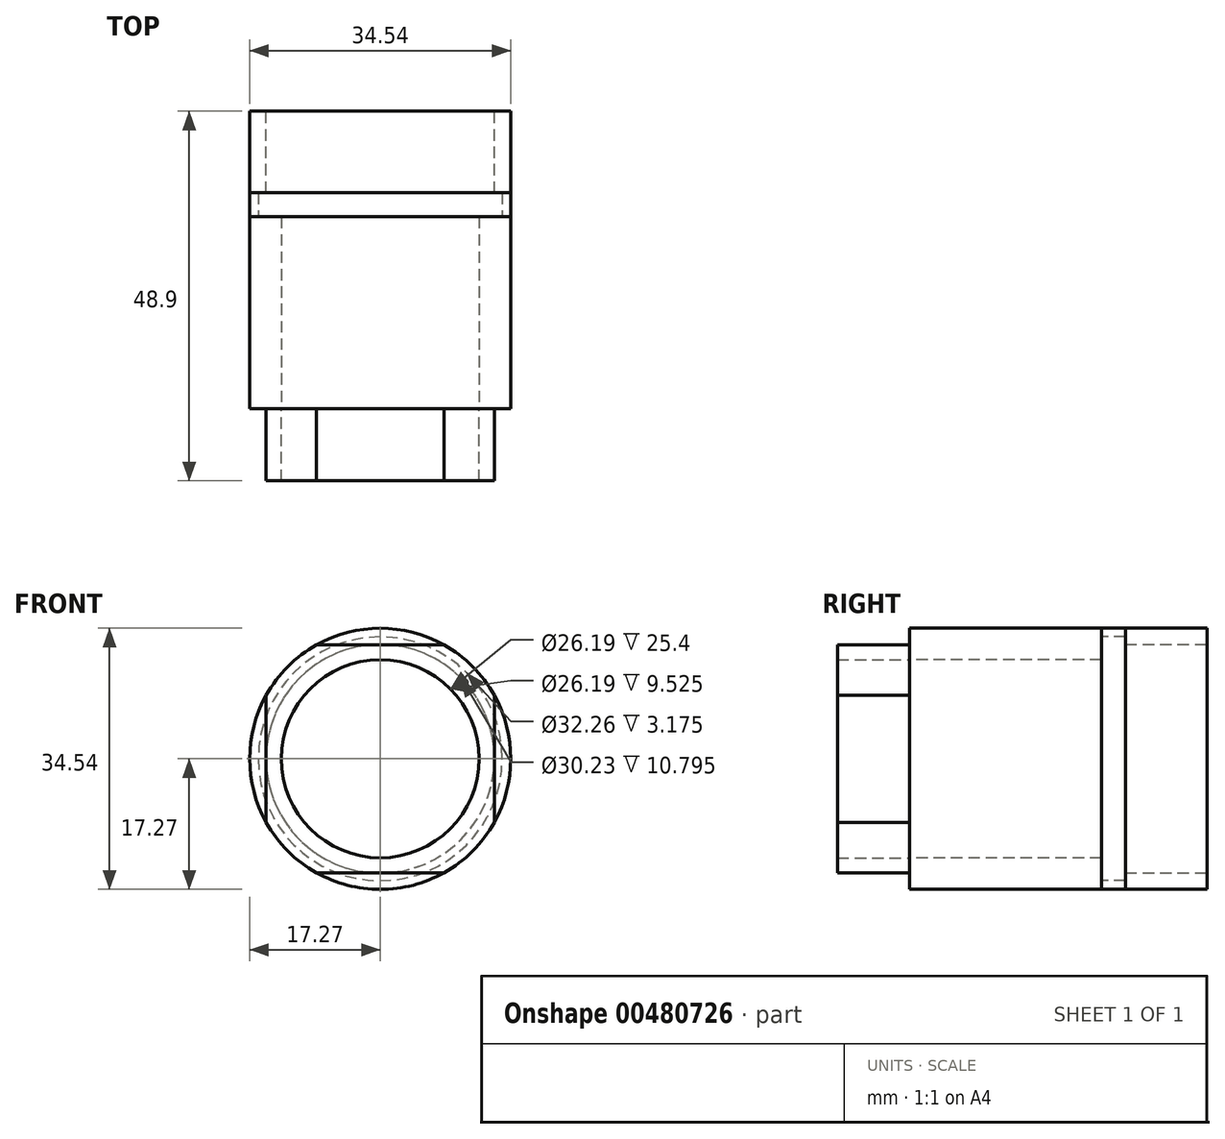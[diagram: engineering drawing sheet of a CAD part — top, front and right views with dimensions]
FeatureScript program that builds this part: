
annotation { "Feature Type Name" : "Feature", "Feature Type Description" : "" }
export const myFeature = defineFeature(function(context is Context, id is Id, definition is map)
    precondition{}
    {
        {
            var Q0;
            Q0=qCreatedBy(makeId("Front.planeOp"),FACE);
            var sketch = newSketch(context, id + "F0", { "sketchPlane" : qUnion([Q0])});
            skCircle(sketch, "E0", {"center": v(0, 0) * mm, "radius": 17.27 * mm});
            skSolve(sketch);
        }
        {
            var Q0;
            Q0 = qSketchRegion(id + "F0", true);
            extrude(context, id + "F1", {"entities" : qUnion([Q0]), "depth" : 10.8 * mm, "offsetDistance" : 25.4 * mm});
        }
        {
            var Q0;
            Q0=makeQuery(id+"F1.opExtrude","CAP_FACE",FACE,{"disambiguationData":[OSD([sQuery(id+"F0.wireOp",EDGE,"E0")])],"isStart":true});
            var sketch = newSketch(context, id + "F2", { "sketchPlane" : qUnion([Q0])});
            skCircle(sketch, "E1", {"center": v(0, 0) * mm, "radius": 15.11 * mm});
            skSolve(sketch);
        }
        {
            var Q0;
            Q0 = qSketchRegion(id + "F2", true);
            extrude(context, id + "F3", {"entities" : qUnion([Q0]), "operationType" : NewBodyOperationType.REMOVE, "endBound" : BoundingType.UP_TO_NEXT, "oppositeDirection" : true, "depth" : 25.4 * mm, "offsetDistance" : 25.4 * mm});
        }
        {
            var Q0;
            Q0=makeQuery(id+"F1.opExtrude","CAP_FACE",FACE,{"disambiguationData":[OSD([sQuery(id+"F0.wireOp",EDGE,"E0")])],"isStart":false});
            var sketch = newSketch(context, id + "F4", { "sketchPlane" : qUnion([Q0])});
            skCircle(sketch, "E2", {"center": v(0, 0) * mm, "radius": 17.27 * mm});
            skSolve(sketch);
        }
        {
            var Q0;
            Q0 = qSketchRegion(id + "F4", true);
            extrude(context, id + "F5", {"entities" : qUnion([Q0]), "depth" : 3.17 * mm, "offsetDistance" : 25.4 * mm});
        }
        {
            var Q0;
            Q0=makeQuery(id+"F5.opExtrude","CAP_FACE",FACE,{"disambiguationData":[OSD([sQuery(id+"F4.wireOp",EDGE,"E2")])],"isStart":false});
            var sketch = newSketch(context, id + "F6", { "sketchPlane" : qUnion([Q0])});
            skCircle(sketch, "E3", {"center": v(0, 0) * mm, "radius": 16.13 * mm});
            skSolve(sketch);
        }
        {
            var Q0;
            Q0 = qSketchRegion(id + "F6", true);
            extrude(context, id + "F7", {"entities" : qUnion([Q0]), "operationType" : NewBodyOperationType.REMOVE, "endBound" : BoundingType.UP_TO_NEXT, "oppositeDirection" : true, "depth" : 25.4 * mm, "offsetDistance" : 25.4 * mm});
        }
        {
            var Q0;
            Q0=makeQuery(id+"F5.opExtrude","CAP_FACE",FACE,{"disambiguationData":[OSD([sQuery(id+"F4.wireOp",EDGE,"E2")])],"isStart":false});
            var sketch = newSketch(context, id + "F8", { "sketchPlane" : qUnion([Q0])});
            skCircle(sketch, "E4", {"center": v(0, 0) * mm, "radius": 17.27 * mm});
            skSolve(sketch);
        }
        {
            var Q0;
            Q0 = qSketchRegion(id + "F8", true);
            extrude(context, id + "F9", {"entities" : qUnion([Q0]), "depth" : 25.4 * mm, "offsetDistance" : 25.4 * mm});
        }
        {
            var Q0;
            Q0=makeQuery(id+"F9.opExtrude","CAP_FACE",FACE,{"disambiguationData":[OSD([sQuery(id+"F8.wireOp",EDGE,"E4")])],"isStart":false});
            var sketch = newSketch(context, id + "F10", { "sketchPlane" : qUnion([Q0])});
            skCircle(sketch, "E5", {"center": v(0, 0) * mm, "radius": 13.1 * mm});
            skSolve(sketch);
        }
        {
            var Q0;
            Q0 = qSketchRegion(id + "F10", true);
            extrude(context, id + "F11", {"entities" : qUnion([Q0]), "operationType" : NewBodyOperationType.REMOVE, "endBound" : BoundingType.UP_TO_NEXT, "oppositeDirection" : true, "depth" : 25.4 * mm, "offsetDistance" : 25.4 * mm});
        }
        {
            var Q0;
            Q0=makeQuery(id+"F9.opExtrude","CAP_FACE",FACE,{"disambiguationData":[OSD([sQuery(id+"F8.wireOp",EDGE,"E4")])],"isStart":false});
            var sketch = newSketch(context, id + "F12", { "sketchPlane" : qUnion([Q0])});
            skCircle(sketch, "E6.cCircle", {"center": v(0, 0) * mm, "radius": 15.08 * mm, "construction": true});
            skLineSegment(sketch, "E6.0", {"start": v(15.08, 8.42) * mm, "end": v(15.08, -8.42) * mm});
            skLineSegment(sketch, "E6.1", {"start": v(8.42, -15.08) * mm, "end": v(-8.42, -15.08) * mm});
            skLineSegment(sketch, "E6.2", {"start": v(-15.08, -8.42) * mm, "end": v(-15.08, 8.42) * mm});
            skLineSegment(sketch, "E6.3", {"start": v(-8.42, 15.08) * mm, "end": v(8.42, 15.08) * mm});
            skPoint(sketch, "E6.0.midPoint", {"position": v(15.08, 0) * mm});
            skPoint(sketch, "E7", {"position": v(15.08, 8.42) * mm});
            skPoint(sketch, "E8", {"position": v(8.42, 15.08) * mm});
            skPoint(sketch, "E9", {"position": v(-8.42, 15.08) * mm});
            skPoint(sketch, "E10", {"position": v(-15.08, 8.42) * mm});
            skPoint(sketch, "E11", {"position": v(-15.08, -8.42) * mm});
            skPoint(sketch, "E12", {"position": v(-8.42, -15.08) * mm});
            skPoint(sketch, "E13", {"position": v(8.42, -15.08) * mm});
            skPoint(sketch, "E14", {"position": v(15.08, -8.42) * mm});
            skPoint(sketch, "E15.orphan", {"position": v(-15.08, 15.08) * mm});
            skPoint(sketch, "E16.orphan", {"position": v(15.08, 15.08) * mm});
            skPoint(sketch, "E17.orphan", {"position": v(15.08, -15.08) * mm});
            skPoint(sketch, "E18.orphan", {"position": v(-15.08, -15.08) * mm});
            skSolve(sketch);
        }
        {
            var Q0;
            Q0 = qSketchRegion(id + "F12", true);
            var Q1;
            {var subQ3=sQuery(id+"F12.wireOp",EDGE,"E6.0");Q1=makeQuery(id+"F12.imprint","IMPRINT",FACE,{"disambiguationData":[TD([[makeQuery(id+"F12.imprint","IMPRINT",EDGE,{"derivedFrom":subQ3}),-1.0]])]});}
            extrude(context, id + "F13", {"entities" : qUnion([Q0, Q1]), "depth" : 9.52 * mm, "offsetDistance" : 25.4 * mm});
        }
    });
